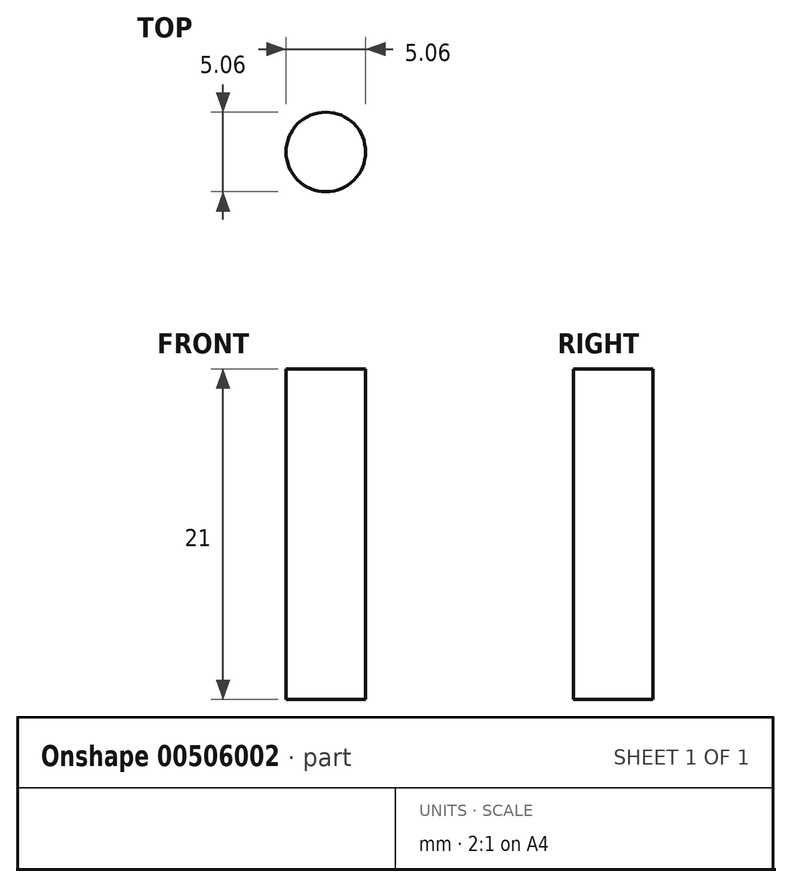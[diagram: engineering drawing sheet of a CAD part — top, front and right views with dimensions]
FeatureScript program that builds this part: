
annotation { "Feature Type Name" : "Feature", "Feature Type Description" : "" }
export const myFeature = defineFeature(function(context is Context, id is Id, definition is map)
    precondition{}
    {
        {
            var Q0;
            Q0=qCreatedBy(makeId("Top.planeOp"),FACE);
            var sketch = newSketch(context, id + "F0", { "sketchPlane" : qUnion([Q0])});
            skCircle(sketch, "E0", {"center": v(0, 0) * mm, "radius": 2.52 * mm});
            skSolve(sketch);
        }
        {
            var Q0;
            Q0 = qSketchRegion(id + "F0", true);
            extrude(context, id + "F1", {"entities" : qUnion([Q0]), "depth" : 21 * mm, "offsetDistance" : 25 * mm});
        }
    });
